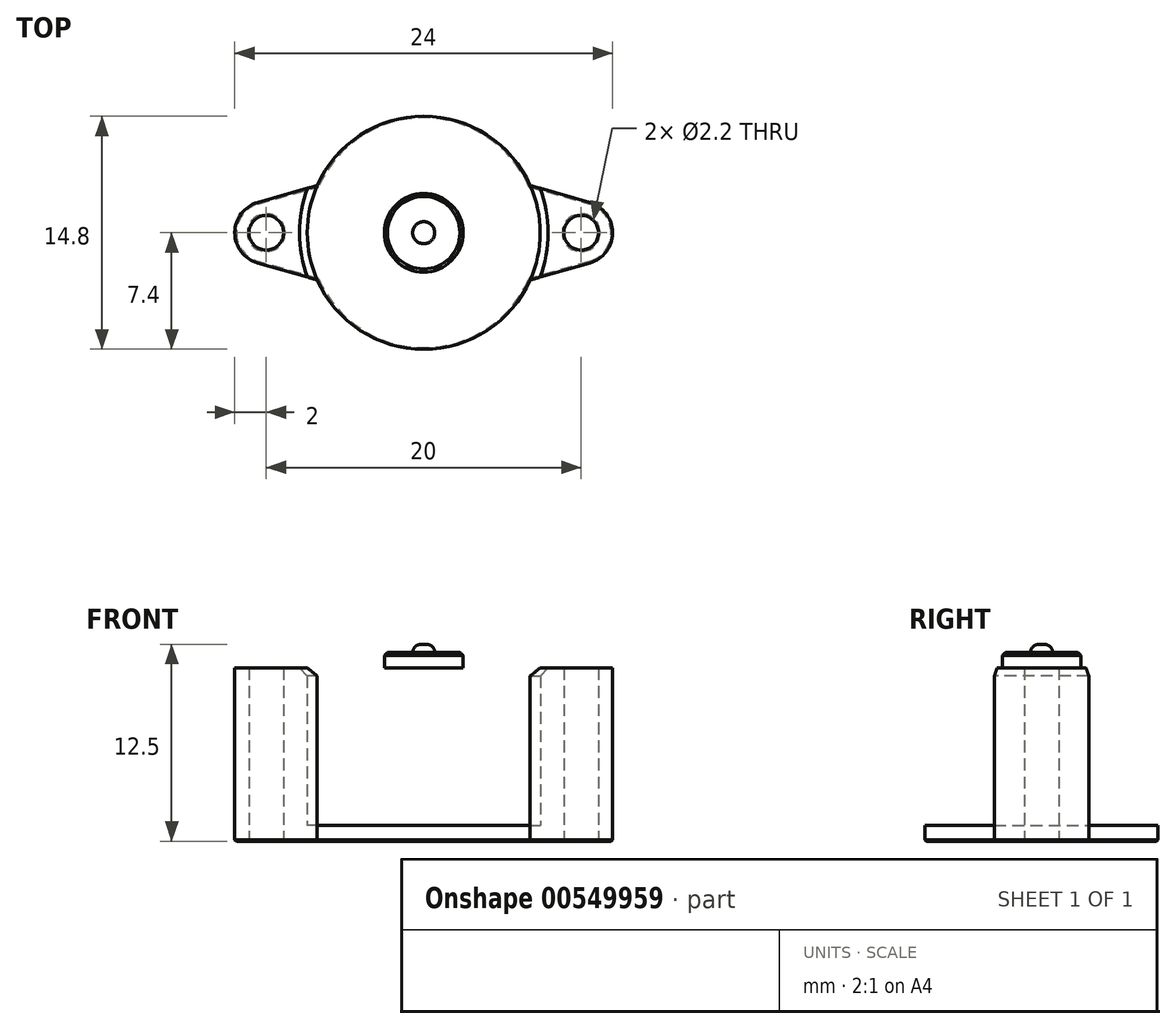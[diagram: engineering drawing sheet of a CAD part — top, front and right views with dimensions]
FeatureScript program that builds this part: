
annotation { "Feature Type Name" : "Feature", "Feature Type Description" : "" }
export const myFeature = defineFeature(function(context is Context, id is Id, definition is map)
    precondition{}
    {
        {
            var Q0;
            Q0=qCreatedBy(makeId("Top.planeOp"),FACE);
            var sketch = newSketch(context, id + "F0", { "sketchPlane" : qUnion([Q0])});
            skCircle(sketch, "E0", {"center": v(-10, 0) * mm, "radius": 1.1 * mm});
            skArc(sketch, "E1", {"start": v(-10.55, -1.92) * mm, "mid": v(-12, 0) * mm, "end": v(-10.55, 1.92) * mm});
            skLineSegment(sketch, "E2", {"start": v(-10.55, 1.92) * mm, "end": v(-6.76, 3) * mm});
            skLineSegment(sketch, "E3", {"start": v(-10.55, -1.92) * mm, "end": v(-6.76, -3) * mm});
            skLineSegment(sketch, "E4.MirrorCS", {"start": v(10.55, -1.92) * mm, "end": v(6.76, -3) * mm});
            skLineSegment(sketch, "E5.MirrorCS", {"start": v(10.55, 1.92) * mm, "end": v(6.76, 3) * mm});
            skArc(sketch, "E6.MirrorCS", {"start": v(10.55, -1.92) * mm, "mid": v(12, 0) * mm, "end": v(10.55, 1.92) * mm});
            skCircle(sketch, "E7.MirrorC", {"center": v(10, 0) * mm, "radius": 1.1 * mm});
            skArc(sketch, "E8", {"start": v(-6.76, 3) * mm, "mid": v(0, 7.4) * mm, "end": v(6.76, 3) * mm});
            skArc(sketch, "E9", {"start": v(6.76, -3) * mm, "mid": v(0, -7.4) * mm, "end": v(-6.76, -3) * mm});
            skSolve(sketch);
        }
        {
            var Q0;
            Q0=makeQuery(id+"F0.imprint","IMPRINT",FACE,{"disambiguationData":[TD([[makeQuery(id+"F0.imprint","IMPRINT",EDGE,{"derivedFrom":sQuery(id+"F0.wireOp",EDGE,"E0")}),-1.0]])]});
            extrude(context, id + "F1", {"entities" : qUnion([Q0]), "depth" : 1 * mm, "offsetDistance" : 25 * mm});
        }
        {
            var Q0;
            Q0=makeQuery(id+"F1.opExtrude","CAP_FACE",FACE,{"disambiguationData":[OSD([sQuery(id+"F0.wireOp",EDGE,"E0"),sQuery(id+"F0.wireOp",EDGE,"E1"),sQuery(id+"F0.wireOp",EDGE,"E2"),sQuery(id+"F0.wireOp",EDGE,"E3"),sQuery(id+"F0.wireOp",EDGE,"E4.MirrorCS"),sQuery(id+"F0.wireOp",EDGE,"E5.MirrorCS"),sQuery(id+"F0.wireOp",EDGE,"E6.MirrorCS"),sQuery(id+"F0.wireOp",EDGE,"E7.MirrorC"),sQuery(id+"F0.wireOp",EDGE,"E8"),sQuery(id+"F0.wireOp",EDGE,"E9")])],"isStart":false});
            var sketch = newSketch(context, id + "F2", { "sketchPlane" : qUnion([Q0])});
            skCircle(sketch, "E10", {"center": v(0, 0) * mm, "radius": 7.4 * mm});
            skSolve(sketch);
        }
        {
            var Q0;
            {var subQ0=sQuery(id+"F2.wireOp",EDGE,"E10");var subQ1=makeQuery(id+"F2.imprint","INTERSECT",VERTEX,{"derivedFrom":[makeQuery(id+"F1.opExtrude","CAP_EDGE",EDGE,{"disambiguationData":[OSD([sQuery(id+"F0.wireOp",EDGE,"E2")])],"isStart":false}),subQ0]});var subQ2=makeQuery(id+"F2.imprint","INTERSECT",VERTEX,{"derivedFrom":[makeQuery(id+"F1.opExtrude","CAP_EDGE",EDGE,{"disambiguationData":[OSD([sQuery(id+"F0.wireOp",EDGE,"E5.MirrorCS")])],"isStart":false}),subQ0]});Q0=makeQuery(id+"F2.imprint","IMPRINT",FACE,{"disambiguationData":[TD([[makeQuery(id+"F2.imprint","IMPRINT",EDGE,{"disambiguationData":[TD([[subQ1,-1.0],[subQ2,1.0]])],"derivedFrom":subQ0}),-1.0]])]});}
            extrude(context, id + "F3", {"entities" : qUnion([Q0]), "operationType" : NewBodyOperationType.ADD, "depth" : 10 * mm, "offsetDistance" : 25 * mm});
        }
        {
            var Q0;
            Q0=makeQuery(id+"F3.opExtrude","CAP_FACE",FACE,{"disambiguationData":[OSD([sQuery(id+"F2.wireOp",EDGE,"E10")])],"isStart":false});
            var sketch = newSketch(context, id + "F4", { "sketchPlane" : qUnion([Q0])});
            skCircle(sketch, "E11", {"center": v(0, 0) * mm, "radius": 2.5 * mm});
            skSolve(sketch);
        }
        {
            var Q0;
            Q0=makeQuery(id+"F4.imprint","IMPRINT",FACE,{"disambiguationData":[TD([[makeQuery(id+"F4.imprint","IMPRINT",EDGE,{"derivedFrom":sQuery(id+"F4.wireOp",EDGE,"E11")}),1.0]])]});
            extrude(context, id + "F5", {"entities" : qUnion([Q0]), "operationType" : NewBodyOperationType.ADD, "depth" : 1 * mm, "offsetDistance" : 25 * mm});
        }
        {
            var Q0;
            Q0=makeQuery(id+"F5.opExtrude","CAP_FACE",FACE,{"disambiguationData":[OSD([sQuery(id+"F4.wireOp",EDGE,"E11")])],"isStart":false});
            var sketch = newSketch(context, id + "F6", { "sketchPlane" : qUnion([Q0])});
            skCircle(sketch, "E12", {"center": v(0, 0) * mm, "radius": 0.7 * mm});
            skSolve(sketch);
        }
        {
            var Q0;
            Q0=makeQuery(id+"F6.imprint","IMPRINT",FACE,{"disambiguationData":[TD([[makeQuery(id+"F6.imprint","IMPRINT",EDGE,{"derivedFrom":sQuery(id+"F6.wireOp",EDGE,"E12")}),1.0]])]});
            extrude(context, id + "F7", {"entities" : qUnion([Q0]), "operationType" : NewBodyOperationType.ADD, "depth" : 0.5 * mm, "offsetDistance" : 25 * mm});
        }
        {
            var Q0;
            Q0=makeQuery(id+"F7.opExtrude","CAP_EDGE",EDGE,{"disambiguationData":[OSD([sQuery(id+"F6.wireOp",EDGE,"E12")])],"isStart":false});
            fillet(context, id + "F8", {"entities" : qUnion([Q0]), "radius" : 0.5 * mm, "tangentPropagation" : true, "allowEdgeOverflow" : false});
        }
        {
            var Q0;
            Q0=makeQuery(id+"F3.opExtrude","CAP_EDGE",EDGE,{"disambiguationData":[OSD([sQuery(id+"F2.wireOp",EDGE,"E10")])],"isStart":false});
            chamfer(context, id + "F9", {"entities" : qUnion([Q0]), "width" : 0.5 * mm, "tangentPropagation" : true});
        }
        {
            var Q0;
            Q0=makeQuery(id+"F1.opExtrude","CAP_FACE",FACE,{"disambiguationData":[OSD([sQuery(id+"F0.wireOp",EDGE,"E0"),sQuery(id+"F0.wireOp",EDGE,"E1"),sQuery(id+"F0.wireOp",EDGE,"E2"),sQuery(id+"F0.wireOp",EDGE,"E3"),sQuery(id+"F0.wireOp",EDGE,"E4.MirrorCS"),sQuery(id+"F0.wireOp",EDGE,"E5.MirrorCS"),sQuery(id+"F0.wireOp",EDGE,"E6.MirrorCS"),sQuery(id+"F0.wireOp",EDGE,"E7.MirrorC"),sQuery(id+"F0.wireOp",EDGE,"E8"),sQuery(id+"F0.wireOp",EDGE,"E9")])],"isStart":true});
            chamfer(context, id + "F10", {"entities" : qUnion([Q0]), "width" : 0.1 * mm, "tangentPropagation" : true});
        }
        {
            var Q0;
            Q0=makeQuery(id+"F5.opExtrude","CAP_EDGE",EDGE,{"disambiguationData":[OSD([sQuery(id+"F4.wireOp",EDGE,"E11")])],"isStart":false});
            chamfer(context, id + "F11", {"entities" : qUnion([Q0]), "width" : 0.2 * mm, "tangentPropagation" : true});
        }
    });
